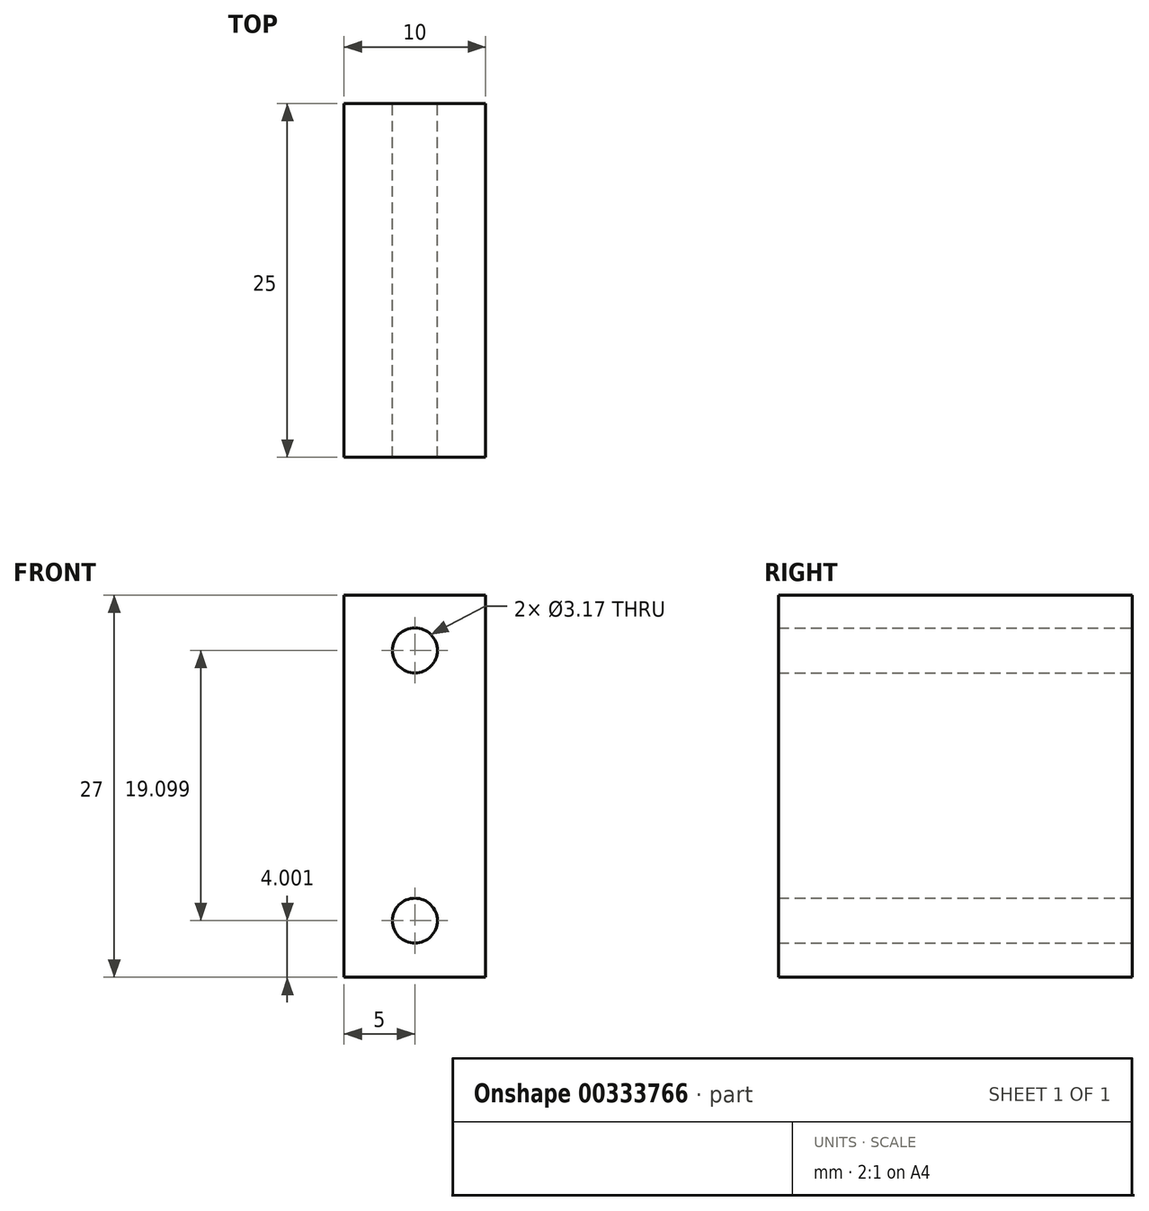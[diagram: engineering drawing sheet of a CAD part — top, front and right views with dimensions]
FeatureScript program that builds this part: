
annotation { "Feature Type Name" : "Feature", "Feature Type Description" : "" }
export const myFeature = defineFeature(function(context is Context, id is Id, definition is map)
    precondition{}
    {
        {
            var Q0;
            Q0=qCreatedBy(makeId("Front.planeOp"),FACE);
            var sketch = newSketch(context, id + "F0", { "sketchPlane" : qUnion([Q0])});
            skLineSegment(sketch, "E0.bottom", {"start": v(0, 12.22) * mm, "end": v(10, 12.22) * mm});
            skLineSegment(sketch, "E0.top", {"start": v(0, -14.78) * mm, "end": v(10, -14.78) * mm});
            skLineSegment(sketch, "E0.left", {"start": v(0, 12.22) * mm, "end": v(0, -14.78) * mm});
            skLineSegment(sketch, "E0.right", {"start": v(10, 12.22) * mm, "end": v(10, -14.78) * mm});
            skCircle(sketch, "E1", {"center": v(5, 8.32) * mm, "radius": 1.59 * mm});
            skCircle(sketch, "E2", {"center": v(5, -10.78) * mm, "radius": 1.59 * mm});
            skSolve(sketch);
        }
        {
            var Q0;
            Q0 = qSketchRegion(id + "F0", true);
            extrude(context, id + "F1", {"entities" : qUnion([Q0]), "depth" : 25 * mm});
        }
    });
